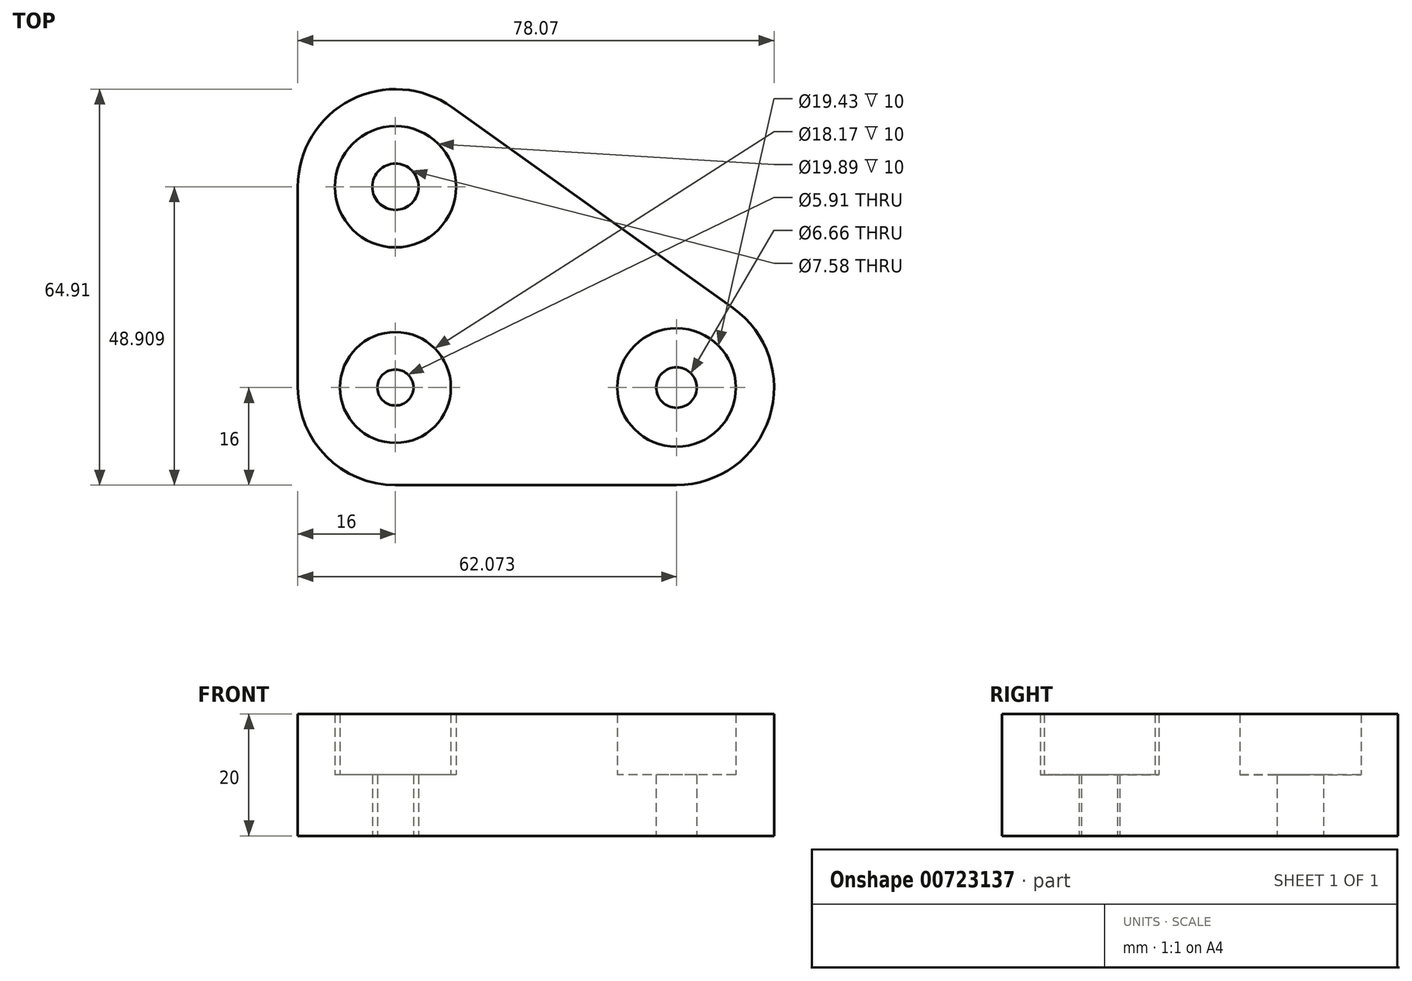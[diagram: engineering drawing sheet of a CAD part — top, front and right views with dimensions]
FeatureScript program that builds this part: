
annotation { "Feature Type Name" : "Feature", "Feature Type Description" : "" }
export const myFeature = defineFeature(function(context is Context, id is Id, definition is map)
    precondition{}
    {
        {
            var Q0;
            Q0=qCreatedBy(makeId("Top.planeOp"),FACE);
            var sketch = newSketch(context, id + "F0", { "sketchPlane" : qUnion([Q0])});
            skLineSegment(sketch, "E0.bottom", {"start": v(16, 0) * mm, "end": v(62.07, 0) * mm});
            skLineSegment(sketch, "E0.left", {"start": v(0, 16) * mm, "end": v(0, 48.9) * mm});
            skLineSegment(sketch, "E1", {"start": v(25.3, 61.93) * mm, "end": v(71.37, 29.02) * mm});
            skPoint(sketch, "E2.visualSharp", {"position": v(0, 0) * mm});
            skArc(sketch, "E2.filletArc", {"start": v(0, 16) * mm, "mid": v(4.69, 4.69) * mm, "end": v(16, 0) * mm});
            skPoint(sketch, "E3.visualSharp", {"position": v(0, 80) * mm});
            skArc(sketch, "E3.filletArc", {"start": v(25.3, 61.93) * mm, "mid": v(8.68, 63.14) * mm, "end": v(0, 48.9) * mm});
            skPoint(sketch, "E4.visualSharp", {"position": v(112, 0) * mm});
            skArc(sketch, "E4.filletArc", {"start": v(62.07, 0) * mm, "mid": v(77.3, 11.12) * mm, "end": v(71.37, 29.02) * mm});
            skCircle(sketch, "E5", {"center": v(16, 16) * mm, "radius": 9.09 * mm});
            skCircle(sketch, "E6", {"center": v(62.07, 16) * mm, "radius": 9.71 * mm});
            skCircle(sketch, "E7", {"center": v(16, 16) * mm, "radius": 2.96 * mm});
            skCircle(sketch, "E8", {"center": v(62.07, 16) * mm, "radius": 3.33 * mm});
            skCircle(sketch, "E9", {"center": v(16, 48.9) * mm, "radius": 9.94 * mm});
            skCircle(sketch, "E10", {"center": v(16, 48.9) * mm, "radius": 3.8 * mm});
            skSolve(sketch);
        }
        {
            var Q0;
            Q0=qSketchRegion(id+"F0",true);
            extrude(context, id + "F1", {"entities" : qUnion([Q0]), "depth" : 20 * mm, "offsetDistance" : 25 * mm});
        }
        {
            var Q0;
            Q0=makeQuery(id+"F0.imprint","IMPRINT",FACE,{"disambiguationData":[TD([[makeQuery(id+"F0.imprint","IMPRINT",EDGE,{"derivedFrom":sQuery(id+"F0.wireOp",EDGE,"E5")}),1.0]])]});
            var Q1;
            Q1=makeQuery(id+"F0.imprint","IMPRINT",FACE,{"disambiguationData":[TD([[makeQuery(id+"F0.imprint","IMPRINT",EDGE,{"derivedFrom":sQuery(id+"F0.wireOp",EDGE,"E9")}),1.0]])]});
            var Q2;
            Q2=makeQuery(id+"F0.imprint","IMPRINT",FACE,{"disambiguationData":[TD([[makeQuery(id+"F0.imprint","IMPRINT",EDGE,{"derivedFrom":sQuery(id+"F0.wireOp",EDGE,"E6")}),1.0]])]});
            extrude(context, id + "F2", {"entities" : qUnion([Q0, Q1, Q2]), "operationType" : NewBodyOperationType.ADD, "depth" : 10 * mm, "offsetDistance" : 25 * mm});
        }
    });
